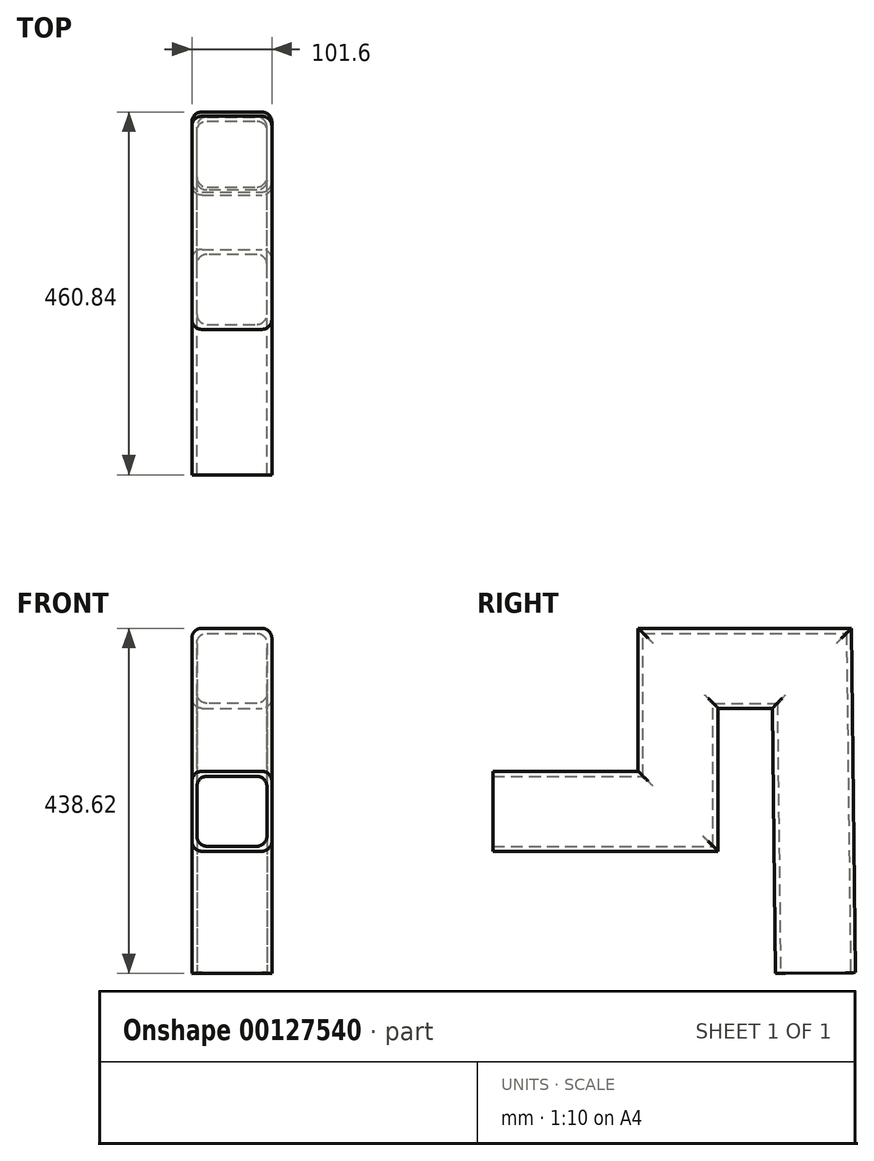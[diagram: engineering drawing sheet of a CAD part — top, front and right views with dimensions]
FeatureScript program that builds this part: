
annotation { "Feature Type Name" : "Feature", "Feature Type Description" : "" }
export const myFeature = defineFeature(function(context is Context, id is Id, definition is map)
    precondition{}
    {
        {
            var Q0;
            Q0=qCreatedBy(makeId("Front.planeOp"),FACE);
            var sketch = newSketch(context, id + "F0", { "sketchPlane" : qUnion([Q0])});
            skLineSegment(sketch, "E0.0", {"start": v(-43.5, -38.1) * mm, "end": v(-43.5, 38.1) * mm});
            skLineSegment(sketch, "E0.1", {"start": v(-30.8, -50.8) * mm, "end": v(45.4, -50.8) * mm});
            skLineSegment(sketch, "E0.2", {"start": v(58.1, -38.1) * mm, "end": v(58.1, 38.1) * mm});
            skLineSegment(sketch, "E0.3", {"start": v(-30.8, 50.8) * mm, "end": v(45.4, 50.8) * mm});
            skLineSegment(sketch, "E1.0", {"start": v(-24.45, 44.45) * mm, "end": v(39.05, 44.45) * mm});
            skLineSegment(sketch, "E1.1", {"start": v(-37.15, -31.75) * mm, "end": v(-37.15, 31.75) * mm});
            skLineSegment(sketch, "E1.2", {"start": v(-24.45, -44.45) * mm, "end": v(39.05, -44.45) * mm});
            skLineSegment(sketch, "E1.3", {"start": v(51.75, -31.75) * mm, "end": v(51.75, 31.75) * mm});
            skPoint(sketch, "E2.visualSharp", {"position": v(-37.15, 44.45) * mm});
            skArc(sketch, "E2.filletArc", {"start": v(-24.45, 44.45) * mm, "mid": v(-33.43, 40.73) * mm, "end": v(-37.15, 31.75) * mm});
            skPoint(sketch, "E3.visualSharp", {"position": v(51.75, 44.45) * mm});
            skArc(sketch, "E3.filletArc", {"start": v(51.75, 31.75) * mm, "mid": v(48.03, 40.73) * mm, "end": v(39.05, 44.45) * mm});
            skPoint(sketch, "E4.visualSharp", {"position": v(51.75, -44.45) * mm});
            skArc(sketch, "E4.filletArc", {"start": v(39.05, -44.45) * mm, "mid": v(48.03, -40.73) * mm, "end": v(51.75, -31.75) * mm});
            skPoint(sketch, "E5.visualSharp", {"position": v(-37.15, -44.45) * mm});
            skArc(sketch, "E5.filletArc", {"start": v(-37.15, -31.75) * mm, "mid": v(-33.43, -40.73) * mm, "end": v(-24.45, -44.45) * mm});
            skPoint(sketch, "E6.visualSharp", {"position": v(-43.5, 50.8) * mm});
            skArc(sketch, "E6.filletArc", {"start": v(-30.8, 50.8) * mm, "mid": v(-39.78, 47.08) * mm, "end": v(-43.5, 38.1) * mm});
            skPoint(sketch, "E7.visualSharp", {"position": v(58.1, 50.8) * mm});
            skArc(sketch, "E7.filletArc", {"start": v(58.1, 38.1) * mm, "mid": v(54.38, 47.08) * mm, "end": v(45.4, 50.8) * mm});
            skPoint(sketch, "E8.visualSharp", {"position": v(58.1, -50.8) * mm});
            skArc(sketch, "E8.filletArc", {"start": v(45.4, -50.8) * mm, "mid": v(54.38, -47.08) * mm, "end": v(58.1, -38.1) * mm});
            skPoint(sketch, "E9.visualSharp", {"position": v(-43.5, -50.8) * mm});
            skArc(sketch, "E9.filletArc", {"start": v(-43.5, -38.1) * mm, "mid": v(-39.78, -47.08) * mm, "end": v(-30.8, -50.8) * mm});
            skSolve(sketch);
        }
        {
            var Q0;
            Q0=qCreatedBy(makeId("Right.planeOp"),FACE);
            var sketch = newSketch(context, id + "F1", { "sketchPlane" : qUnion([Q0])});
            skLineSegment(sketch, "E10", {"start": v(0, 0) * mm, "end": v(235.5, 0) * mm});
            skLineSegment(sketch, "E11", {"start": v(235.5, 0) * mm, "end": v(235.5, 181.7) * mm});
            skLineSegment(sketch, "E12", {"start": v(235.5, 181.7) * mm, "end": v(405.36, 181.7) * mm});
            skLineSegment(sketch, "E13", {"start": v(405.36, 181.7) * mm, "end": v(410.04, -205.51) * mm});
            skSolve(sketch);
        }
        {
            var Q0;
            Q0 = qSketchRegion(id + "F0", true);
            var Q1;
            Q1 = qConstructionFilter(qBodyType(qCreatedBy(id + "F1" ,EDGE), BodyType.WIRE), ConstructionObject.NO);
            sweep(context, id + "F2", {"profiles" : qUnion([Q0]), "path" : qUnion([Q1])});
        }
    });
